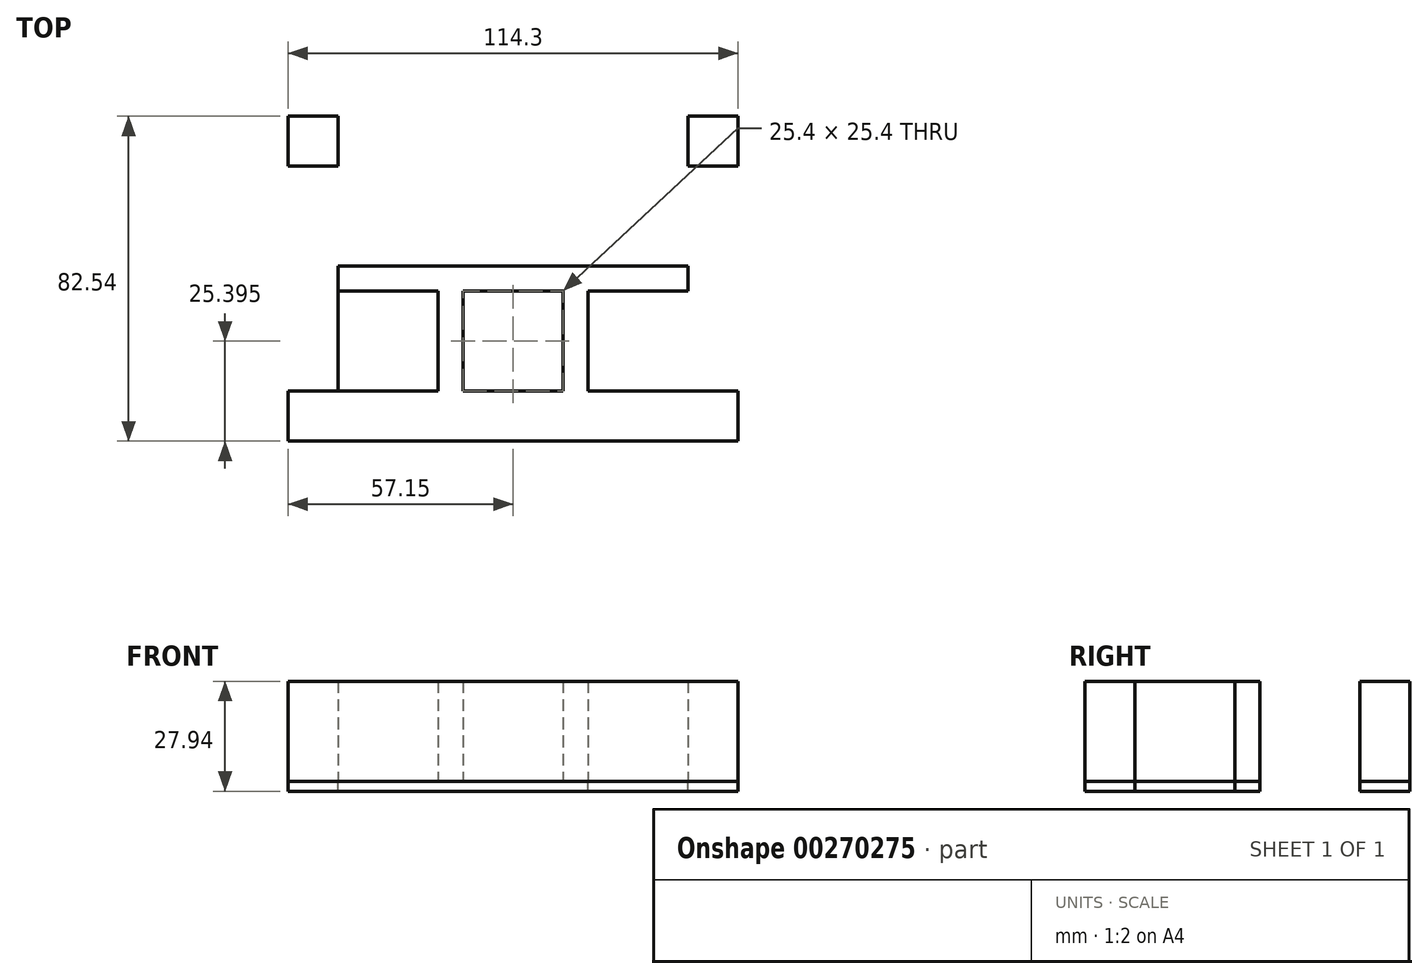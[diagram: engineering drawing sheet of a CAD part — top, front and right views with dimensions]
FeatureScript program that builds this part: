
annotation { "Feature Type Name" : "Feature", "Feature Type Description" : "" }
export const myFeature = defineFeature(function(context is Context, id is Id, definition is map)
    precondition{}
    {
        {
            var Q0;
            Q0=qCreatedBy(makeId("Top.planeOp"),FACE);
            var sketch = newSketch(context, id + "F0", { "sketchPlane" : qUnion([Q0])});
            skLineSegment(sketch, "E0.bottom", {"start": v(57.15, 41.28) * mm, "end": v(-57.15, 41.28) * mm});
            skLineSegment(sketch, "E0.top", {"start": v(57.15, -41.27) * mm, "end": v(-57.15, -41.27) * mm});
            skLineSegment(sketch, "E0.left", {"start": v(57.15, 41.28) * mm, "end": v(57.15, -41.27) * mm});
            skLineSegment(sketch, "E0.right", {"start": v(-57.15, 41.28) * mm, "end": v(-57.15, -41.27) * mm});
            skPoint(sketch, "E0.middle", {"position": v(0, 0) * mm});
            skLineSegment(sketch, "E1", {"start": v(-57.15, 41.28) * mm, "end": v(-57.15, 28.58) * mm});
            skLineSegment(sketch, "E2", {"start": v(-57.15, 28.58) * mm, "end": v(57.15, 28.57) * mm});
            skLineSegment(sketch, "E3", {"start": v(-57.15, -41.27) * mm, "end": v(-57.15, -28.57) * mm});
            skLineSegment(sketch, "E4", {"start": v(-57.15, -28.58) * mm, "end": v(57.15, -28.58) * mm});
            skLineSegment(sketch, "E5", {"start": v(57.15, 41.28) * mm, "end": v(44.45, 41.28) * mm});
            skLineSegment(sketch, "E6", {"start": v(-57.15, 41.28) * mm, "end": v(-44.45, 41.28) * mm});
            skLineSegment(sketch, "E7", {"start": v(-44.45, 41.28) * mm, "end": v(-44.45, -41.27) * mm});
            skLineSegment(sketch, "E8", {"start": v(44.45, 41.28) * mm, "end": v(44.45, -41.27) * mm});
            skLineSegment(sketch, "E9", {"start": v(44.45, 28.58) * mm, "end": v(44.45, 3.18) * mm});
            skLineSegment(sketch, "E10", {"start": v(44.45, 3.18) * mm, "end": v(-44.45, 3.18) * mm});
            skLineSegment(sketch, "E11", {"start": v(44.45, -28.57) * mm, "end": v(44.45, -3.17) * mm});
            skLineSegment(sketch, "E12", {"start": v(44.45, -3.17) * mm, "end": v(-44.45, -3.17) * mm});
            skLineSegment(sketch, "E13", {"start": v(-44.45, 28.58) * mm, "end": v(-19.05, 28.57) * mm});
            skLineSegment(sketch, "E14", {"start": v(-19.05, 28.57) * mm, "end": v(-12.7, 28.57) * mm});
            skLineSegment(sketch, "E15", {"start": v(-19.05, 28.58) * mm, "end": v(-19.05, -28.57) * mm});
            skLineSegment(sketch, "E16", {"start": v(-12.7, 28.58) * mm, "end": v(-12.7, -28.57) * mm});
            skLineSegment(sketch, "E17", {"start": v(-12.7, 28.57) * mm, "end": v(12.7, 28.57) * mm});
            skLineSegment(sketch, "E18", {"start": v(12.7, 28.58) * mm, "end": v(12.7, -28.58) * mm});
            skLineSegment(sketch, "E19", {"start": v(12.7, 28.57) * mm, "end": v(19.05, 28.57) * mm});
            skLineSegment(sketch, "E20", {"start": v(19.05, 28.58) * mm, "end": v(19.05, -28.58) * mm});
            skSolve(sketch);
        }
        {
            var Q0;
            {var subQ0=sQuery(id+"F0.wireOp",EDGE,"E1");Q0=makeQuery(id+"F0.imprint","IMPRINT",FACE,{"disambiguationData":[TD([[makeQuery(id+"F0.imprint","IMPRINT",EDGE,{"derivedFrom":subQ0}),1.0]])]});}
            var Q1;
            {var subQ4=sQuery(id+"F0.wireOp",EDGE,"E0.right");Q1=makeQuery(id+"F0.imprint","IMPRINT",FACE,{"disambiguationData":[TD([[makeQuery(id+"F0.imprint","IMPRINT",EDGE,{"derivedFrom":subQ4}),1.0]])]});}
            var Q2;
            {var subQ0=sQuery(id+"F0.wireOp",EDGE,"E3");Q2=makeQuery(id+"F0.imprint","IMPRINT",FACE,{"disambiguationData":[TD([[makeQuery(id+"F0.imprint","IMPRINT",EDGE,{"derivedFrom":subQ0}),-1.0]])]});}
            var Q3;
            {var subQ3=sQuery(id+"F0.wireOp",EDGE,"E7");var subQ4=sQuery(id+"F0.wireOp",EDGE,"E0.top");var subQ5=makeQuery(id+"F0.imprint","INTERSECT",VERTEX,{"derivedFrom":[subQ4,subQ3]});Q3=makeQuery(id+"F0.imprint","IMPRINT",FACE,{"disambiguationData":[TD([[makeQuery(id+"F0.imprint","IMPRINT",EDGE,{"disambiguationData":[TD([[subQ5,1.0]])],"derivedFrom":subQ4}),-1.0]])]});}
            var Q4;
            {var subQ0=sQuery(id+"F0.wireOp",EDGE,"E0.left");var subQ1=sQuery(id+"F0.wireOp",EDGE,"E0.top");var subQ2=makeQuery(id+"F0.imprint","INTERSECT",VERTEX,{"derivedFrom":[subQ1,subQ0]});Q4=makeQuery(id+"F0.imprint","IMPRINT",FACE,{"disambiguationData":[TD([[makeQuery(id+"F0.imprint","IMPRINT",EDGE,{"disambiguationData":[TD([[subQ2,-1.0]])],"derivedFrom":subQ1}),-1.0]])]});}
            var Q5;
            {var subQ0=sQuery(id+"F0.wireOp",EDGE,"E9");Q5=makeQuery(id+"F0.imprint","IMPRINT",FACE,{"disambiguationData":[TD([[makeQuery(id+"F0.imprint","IMPRINT",EDGE,{"derivedFrom":subQ0}),1.0]])]});}
            var Q6;
            {var subQ0=sQuery(id+"F0.wireOp",EDGE,"E5");Q6=makeQuery(id+"F0.imprint","IMPRINT",FACE,{"disambiguationData":[TD([[makeQuery(id+"F0.imprint","IMPRINT",EDGE,{"derivedFrom":subQ0}),1.0]])]});}
            var Q7;
            {var subQ1=sQuery(id+"F0.wireOp",EDGE,"E0.bottom");Q7=makeQuery(id+"F0.imprint","IMPRINT",FACE,{"disambiguationData":[TD([[makeQuery(id+"F0.imprint","IMPRINT",EDGE,{"derivedFrom":subQ1}),1.0]])]});}
            var Q8;
            {var subQ5=sQuery(id+"F0.wireOp",EDGE,"E19");Q8=makeQuery(id+"F0.imprint","IMPRINT",FACE,{"disambiguationData":[TD([[makeQuery(id+"F0.imprint","IMPRINT",EDGE,{"derivedFrom":subQ5}),-1.0]])]});}
            var Q9;
            {var subQ0=sQuery(id+"F0.wireOp",EDGE,"E20");var subQ1=sQuery(id+"F0.wireOp",EDGE,"E10");var subQ2=makeQuery(id+"F0.imprint","INTERSECT",VERTEX,{"derivedFrom":[subQ1,subQ0]});Q9=makeQuery(id+"F0.imprint","IMPRINT",FACE,{"disambiguationData":[TD([[makeQuery(id+"F0.imprint","IMPRINT",EDGE,{"disambiguationData":[TD([[subQ2,-1.0]])],"derivedFrom":subQ1}),1.0]])]});}
            var Q10;
            {var subQ0=sQuery(id+"F0.wireOp",EDGE,"E18");var subQ1=sQuery(id+"F0.wireOp",EDGE,"E4");var subQ2=makeQuery(id+"F0.imprint","INTERSECT",VERTEX,{"derivedFrom":[subQ1,subQ0]});Q10=makeQuery(id+"F0.imprint","IMPRINT",FACE,{"disambiguationData":[TD([[makeQuery(id+"F0.imprint","IMPRINT",EDGE,{"disambiguationData":[TD([[subQ2,-1.0]])],"derivedFrom":subQ1}),1.0]])]});}
            var Q11;
            {var subQ5=sQuery(id+"F0.wireOp",EDGE,"E14");Q11=makeQuery(id+"F0.imprint","IMPRINT",FACE,{"disambiguationData":[TD([[makeQuery(id+"F0.imprint","IMPRINT",EDGE,{"derivedFrom":subQ5}),-1.0]])]});}
            var Q12;
            {var subQ0=sQuery(id+"F0.wireOp",EDGE,"E16");var subQ1=sQuery(id+"F0.wireOp",EDGE,"E10");var subQ2=makeQuery(id+"F0.imprint","INTERSECT",VERTEX,{"derivedFrom":[subQ1,subQ0]});Q12=makeQuery(id+"F0.imprint","IMPRINT",FACE,{"disambiguationData":[TD([[makeQuery(id+"F0.imprint","IMPRINT",EDGE,{"disambiguationData":[TD([[subQ2,-1.0]])],"derivedFrom":subQ1}),1.0]])]});}
            var Q13;
            {var subQ0=sQuery(id+"F0.wireOp",EDGE,"E15");var subQ1=sQuery(id+"F0.wireOp",EDGE,"E4");var subQ2=makeQuery(id+"F0.imprint","INTERSECT",VERTEX,{"derivedFrom":[subQ1,subQ0]});Q13=makeQuery(id+"F0.imprint","IMPRINT",FACE,{"disambiguationData":[TD([[makeQuery(id+"F0.imprint","IMPRINT",EDGE,{"disambiguationData":[TD([[subQ2,-1.0]])],"derivedFrom":subQ1}),1.0]])]});}
            var Q14;
            {var subQ0=sQuery(id+"F0.wireOp",EDGE,"E10");var subQ1=sQuery(id+"F0.wireOp",EDGE,"E7");var subQ2=makeQuery(id+"F0.imprint","INTERSECT",VERTEX,{"derivedFrom":[subQ1,subQ0]});Q14=makeQuery(id+"F0.imprint","IMPRINT",FACE,{"disambiguationData":[TD([[makeQuery(id+"F0.imprint","IMPRINT",EDGE,{"disambiguationData":[TD([[subQ2,-1.0]])],"derivedFrom":subQ1}),1.0]])]});}
            var Q15;
            {var subQ0=sQuery(id+"F0.wireOp",EDGE,"E18");var subQ1=sQuery(id+"F0.wireOp",EDGE,"E10");var subQ2=makeQuery(id+"F0.imprint","INTERSECT",VERTEX,{"derivedFrom":[subQ1,subQ0]});Q15=makeQuery(id+"F0.imprint","IMPRINT",FACE,{"disambiguationData":[TD([[makeQuery(id+"F0.imprint","IMPRINT",EDGE,{"disambiguationData":[TD([[subQ2,-1.0]])],"derivedFrom":subQ1}),1.0]])]});}
            var Q16;
            {var subQ0=sQuery(id+"F0.wireOp",EDGE,"E10");var subQ5=sQuery(id+"F0.wireOp",EDGE,"E20");var subQ6=makeQuery(id+"F0.imprint","INTERSECT",VERTEX,{"derivedFrom":[subQ0,subQ5]});Q16=makeQuery(id+"F0.imprint","IMPRINT",FACE,{"disambiguationData":[TD([[makeQuery(id+"F0.imprint","IMPRINT",EDGE,{"disambiguationData":[TD([[subQ6,-1.0]])],"derivedFrom":subQ5}),1.0]])]});}
            extrude(context, id + "F1", {"entities" : qUnion([Q0, Q1, Q2, Q3, Q4, Q5, Q6, Q7, Q8, Q9, Q10, Q11, Q12, Q13, Q14, Q15, Q16]), "depth" : 25.4 * mm});
        }
        {
            var Q0;
            {var subQ3=sQuery(id+"F0.wireOp",EDGE,"E13");Q0=makeQuery(id+"F0.imprint","IMPRINT",FACE,{"disambiguationData":[TD([[makeQuery(id+"F0.imprint","IMPRINT",EDGE,{"derivedFrom":subQ3}),-1.0]])]});}
            var Q1;
            {var subQ4=sQuery(id+"F0.wireOp",EDGE,"E0.right");Q1=makeQuery(id+"F0.imprint","IMPRINT",FACE,{"disambiguationData":[TD([[makeQuery(id+"F0.imprint","IMPRINT",EDGE,{"derivedFrom":subQ4}),1.0]])]});}
            var Q2;
            {var subQ0=sQuery(id+"F0.wireOp",EDGE,"E3");Q2=makeQuery(id+"F0.imprint","IMPRINT",FACE,{"disambiguationData":[TD([[makeQuery(id+"F0.imprint","IMPRINT",EDGE,{"derivedFrom":subQ0}),-1.0]])]});}
            var Q3;
            {var subQ3=sQuery(id+"F0.wireOp",EDGE,"E7");var subQ4=sQuery(id+"F0.wireOp",EDGE,"E0.top");var subQ5=makeQuery(id+"F0.imprint","INTERSECT",VERTEX,{"derivedFrom":[subQ4,subQ3]});Q3=makeQuery(id+"F0.imprint","IMPRINT",FACE,{"disambiguationData":[TD([[makeQuery(id+"F0.imprint","IMPRINT",EDGE,{"disambiguationData":[TD([[subQ5,1.0]])],"derivedFrom":subQ4}),-1.0]])]});}
            var Q4;
            {var subQ0=sQuery(id+"F0.wireOp",EDGE,"E0.left");var subQ1=sQuery(id+"F0.wireOp",EDGE,"E0.top");var subQ2=makeQuery(id+"F0.imprint","INTERSECT",VERTEX,{"derivedFrom":[subQ1,subQ0]});Q4=makeQuery(id+"F0.imprint","IMPRINT",FACE,{"disambiguationData":[TD([[makeQuery(id+"F0.imprint","IMPRINT",EDGE,{"disambiguationData":[TD([[subQ2,-1.0]])],"derivedFrom":subQ1}),-1.0]])]});}
            var Q5;
            {var subQ0=sQuery(id+"F0.wireOp",EDGE,"E9");Q5=makeQuery(id+"F0.imprint","IMPRINT",FACE,{"disambiguationData":[TD([[makeQuery(id+"F0.imprint","IMPRINT",EDGE,{"derivedFrom":subQ0}),1.0]])]});}
            var Q6;
            {var subQ0=sQuery(id+"F0.wireOp",EDGE,"E11");Q6=makeQuery(id+"F0.imprint","IMPRINT",FACE,{"disambiguationData":[TD([[makeQuery(id+"F0.imprint","IMPRINT",EDGE,{"derivedFrom":subQ0}),1.0]])]});}
            var Q7;
            {var subQ0=sQuery(id+"F0.wireOp",EDGE,"E15");var subQ1=sQuery(id+"F0.wireOp",EDGE,"E4");var subQ2=makeQuery(id+"F0.imprint","INTERSECT",VERTEX,{"derivedFrom":[subQ1,subQ0]});Q7=makeQuery(id+"F0.imprint","IMPRINT",FACE,{"disambiguationData":[TD([[makeQuery(id+"F0.imprint","IMPRINT",EDGE,{"disambiguationData":[TD([[subQ2,1.0]])],"derivedFrom":subQ1}),1.0]])]});}
            var Q8;
            {var subQ5=sQuery(id+"F0.wireOp",EDGE,"E17");Q8=makeQuery(id+"F0.imprint","IMPRINT",FACE,{"disambiguationData":[TD([[makeQuery(id+"F0.imprint","IMPRINT",EDGE,{"derivedFrom":subQ5}),-1.0]])]});}
            var Q9;
            {var subQ0=sQuery(id+"F0.wireOp",EDGE,"E9");Q9=makeQuery(id+"F0.imprint","IMPRINT",FACE,{"disambiguationData":[TD([[makeQuery(id+"F0.imprint","IMPRINT",EDGE,{"derivedFrom":subQ0}),-1.0]])]});}
            var Q10;
            {var subQ1=sQuery(id+"F0.wireOp",EDGE,"E0.bottom");Q10=makeQuery(id+"F0.imprint","IMPRINT",FACE,{"disambiguationData":[TD([[makeQuery(id+"F0.imprint","IMPRINT",EDGE,{"derivedFrom":subQ1}),1.0]])]});}
            var Q11;
            {var subQ0=sQuery(id+"F0.wireOp",EDGE,"E5");Q11=makeQuery(id+"F0.imprint","IMPRINT",FACE,{"disambiguationData":[TD([[makeQuery(id+"F0.imprint","IMPRINT",EDGE,{"derivedFrom":subQ0}),1.0]])]});}
            var Q12;
            {var subQ0=sQuery(id+"F0.wireOp",EDGE,"E1");Q12=makeQuery(id+"F0.imprint","IMPRINT",FACE,{"disambiguationData":[TD([[makeQuery(id+"F0.imprint","IMPRINT",EDGE,{"derivedFrom":subQ0}),1.0]])]});}
            var Q13;
            {var subQ0=sQuery(id+"F0.wireOp",EDGE,"E10");var subQ1=sQuery(id+"F0.wireOp",EDGE,"E7");var subQ2=makeQuery(id+"F0.imprint","INTERSECT",VERTEX,{"derivedFrom":[subQ1,subQ0]});Q13=makeQuery(id+"F0.imprint","IMPRINT",FACE,{"disambiguationData":[TD([[makeQuery(id+"F0.imprint","IMPRINT",EDGE,{"disambiguationData":[TD([[subQ2,-1.0]])],"derivedFrom":subQ1}),1.0]])]});}
            var Q14;
            {var subQ0=sQuery(id+"F0.wireOp",EDGE,"E16");var subQ1=sQuery(id+"F0.wireOp",EDGE,"E4");var subQ2=makeQuery(id+"F0.imprint","INTERSECT",VERTEX,{"derivedFrom":[subQ1,subQ0]});Q14=makeQuery(id+"F0.imprint","IMPRINT",FACE,{"disambiguationData":[TD([[makeQuery(id+"F0.imprint","IMPRINT",EDGE,{"disambiguationData":[TD([[subQ2,-1.0]])],"derivedFrom":subQ1}),1.0]])]});}
            var Q15;
            {var subQ0=sQuery(id+"F0.wireOp",EDGE,"E18");var subQ1=sQuery(id+"F0.wireOp",EDGE,"E4");var subQ2=makeQuery(id+"F0.imprint","INTERSECT",VERTEX,{"derivedFrom":[subQ1,subQ0]});Q15=makeQuery(id+"F0.imprint","IMPRINT",FACE,{"disambiguationData":[TD([[makeQuery(id+"F0.imprint","IMPRINT",EDGE,{"disambiguationData":[TD([[subQ2,-1.0]])],"derivedFrom":subQ1}),1.0]])]});}
            var Q16;
            {var subQ0=sQuery(id+"F0.wireOp",EDGE,"E15");var subQ1=sQuery(id+"F0.wireOp",EDGE,"E4");var subQ2=makeQuery(id+"F0.imprint","INTERSECT",VERTEX,{"derivedFrom":[subQ1,subQ0]});Q16=makeQuery(id+"F0.imprint","IMPRINT",FACE,{"disambiguationData":[TD([[makeQuery(id+"F0.imprint","IMPRINT",EDGE,{"disambiguationData":[TD([[subQ2,-1.0]])],"derivedFrom":subQ1}),1.0]])]});}
            var Q17;
            {var subQ0=sQuery(id+"F0.wireOp",EDGE,"E16");var subQ1=sQuery(id+"F0.wireOp",EDGE,"E10");var subQ2=makeQuery(id+"F0.imprint","INTERSECT",VERTEX,{"derivedFrom":[subQ1,subQ0]});Q17=makeQuery(id+"F0.imprint","IMPRINT",FACE,{"disambiguationData":[TD([[makeQuery(id+"F0.imprint","IMPRINT",EDGE,{"disambiguationData":[TD([[subQ2,-1.0]])],"derivedFrom":subQ1}),1.0]])]});}
            var Q18;
            {var subQ5=sQuery(id+"F0.wireOp",EDGE,"E14");Q18=makeQuery(id+"F0.imprint","IMPRINT",FACE,{"disambiguationData":[TD([[makeQuery(id+"F0.imprint","IMPRINT",EDGE,{"derivedFrom":subQ5}),-1.0]])]});}
            var Q19;
            {var subQ0=sQuery(id+"F0.wireOp",EDGE,"E18");var subQ1=sQuery(id+"F0.wireOp",EDGE,"E10");var subQ2=makeQuery(id+"F0.imprint","INTERSECT",VERTEX,{"derivedFrom":[subQ1,subQ0]});Q19=makeQuery(id+"F0.imprint","IMPRINT",FACE,{"disambiguationData":[TD([[makeQuery(id+"F0.imprint","IMPRINT",EDGE,{"disambiguationData":[TD([[subQ2,-1.0]])],"derivedFrom":subQ1}),1.0]])]});}
            var Q20;
            {var subQ0=sQuery(id+"F0.wireOp",EDGE,"E20");var subQ1=sQuery(id+"F0.wireOp",EDGE,"E10");var subQ2=makeQuery(id+"F0.imprint","INTERSECT",VERTEX,{"derivedFrom":[subQ1,subQ0]});Q20=makeQuery(id+"F0.imprint","IMPRINT",FACE,{"disambiguationData":[TD([[makeQuery(id+"F0.imprint","IMPRINT",EDGE,{"disambiguationData":[TD([[subQ2,-1.0]])],"derivedFrom":subQ1}),1.0]])]});}
            var Q21;
            {var subQ0=sQuery(id+"F0.wireOp",EDGE,"E10");var subQ5=sQuery(id+"F0.wireOp",EDGE,"E20");var subQ6=makeQuery(id+"F0.imprint","INTERSECT",VERTEX,{"derivedFrom":[subQ0,subQ5]});Q21=makeQuery(id+"F0.imprint","IMPRINT",FACE,{"disambiguationData":[TD([[makeQuery(id+"F0.imprint","IMPRINT",EDGE,{"disambiguationData":[TD([[subQ6,-1.0]])],"derivedFrom":subQ5}),1.0]])]});}
            var Q22;
            {var subQ5=sQuery(id+"F0.wireOp",EDGE,"E19");Q22=makeQuery(id+"F0.imprint","IMPRINT",FACE,{"disambiguationData":[TD([[makeQuery(id+"F0.imprint","IMPRINT",EDGE,{"derivedFrom":subQ5}),-1.0]])]});}
            extrude(context, id + "F2", {"entities" : qUnion([Q0, Q1, Q2, Q3, Q4, Q5, Q6, Q7, Q8, Q9, Q10, Q11, Q12, Q13, Q14, Q15, Q16, Q17, Q18, Q19, Q20, Q21, Q22]), "oppositeDirection" : true, "depth" : 2.54 * mm});
        }
    });
